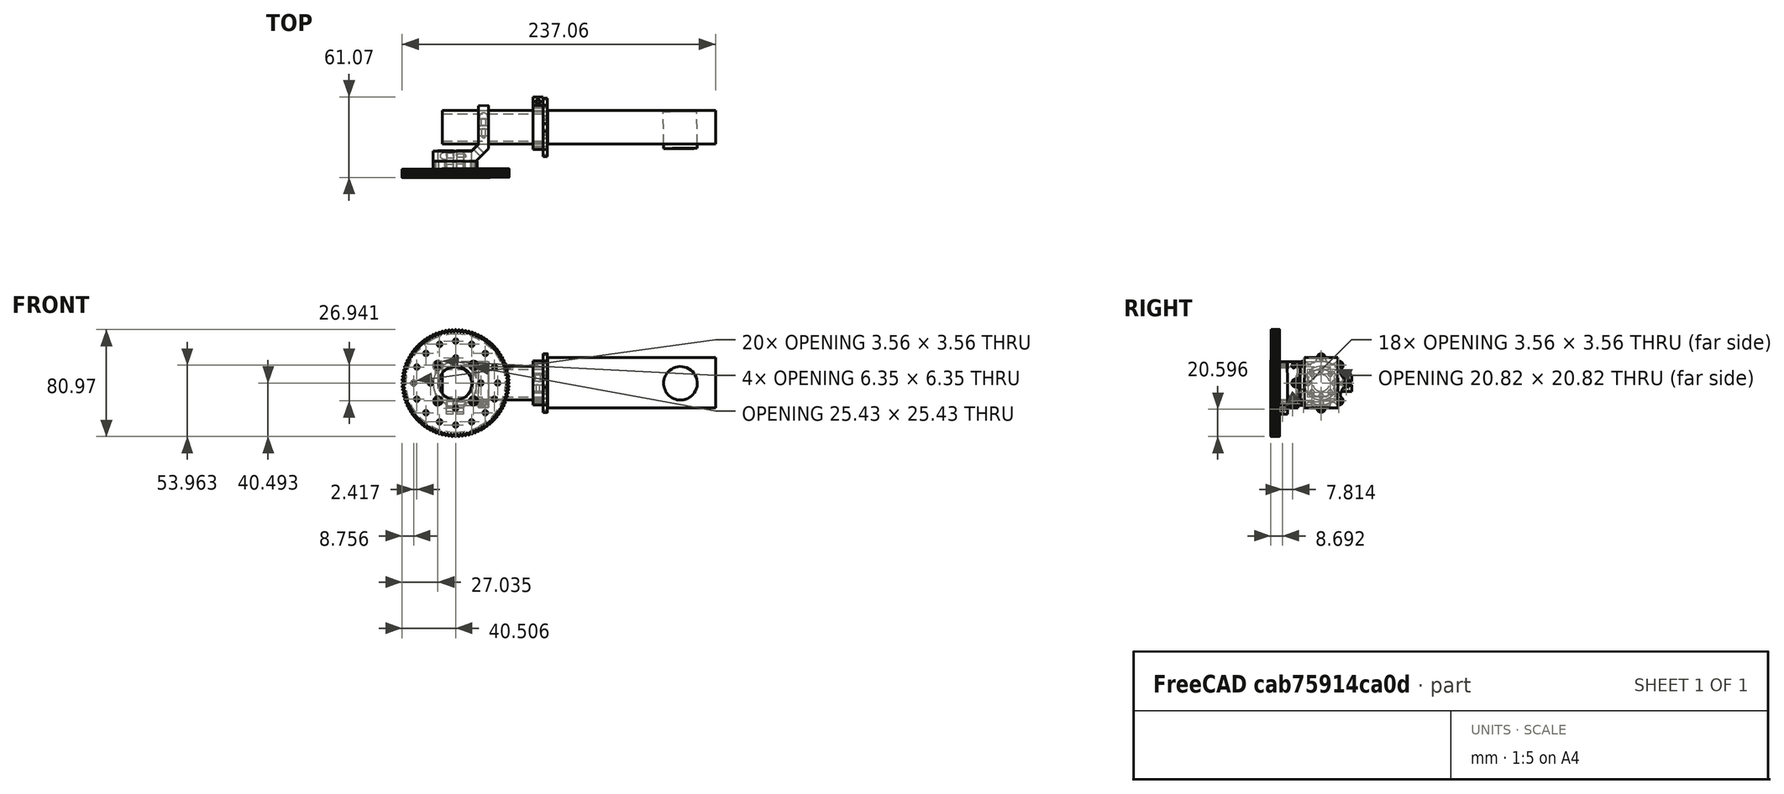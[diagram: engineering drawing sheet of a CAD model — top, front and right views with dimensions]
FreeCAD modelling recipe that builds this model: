
FCSTD DOCUMENT  (FreeCAD 0.15R4671 (Git))
Label: elbow
License: All rights reserved
LicenseURL: http://en.wikipedia.org/wiki/All_rights_reserved
objects: Part::Feature×6, Part::Box×1, Part::Cylinder×1
note: 8 computed .brp shape members not serialized (recipe doc carries the construction recipe); baked Part::Feature solids carry a one-line shape summary decoded from their .brp

FEATURE [Part::Feature] Part__Feature  label="635104"
  Placement = pos=(66.1451,36.2578,0) rot=(0,0,1;1.5708rad)
  shape: bbox 76.2 x 25.39 x 25.39 mm, 6 faces (baked)
FEATURE [Part::Feature] Part__Feature001  label="545354"
  Placement = pos=(66.1451,36.2578,0) rot=(0,0,1;1.5708rad)
  shape: bbox 7.62 x 39.7 x 33.29 mm, 45 faces (baked)
FEATURE [Part::Box] Box  label="Cube"
  Height = 38.1
  Length = 127
  Placement = pos=(69.559,23.557,-18.7554) rot=(0,0,1;0rad)
  Width = 25.4
FEATURE [Part::Cylinder] Cylinder
  Angle = 360
  Height = 27.94
  Placement = pos=(170.027,20.321,-0.182765) rot=(0.584444,-0.573279,-0.574261;4.18169rad)
  Radius = 12.7
FEATURE [Part::Feature] Part__Feature004  label="545388"
  Placement = pos=(69.3201,36.2578,0) rot=(0,0,1;1.5708rad)
  shape: bbox 3.175 x 44.37 x 44.37 mm, 73 faces (baked)
FEATURE [Part::Feature] Part__Feature005  label="545464"
  Placement = pos=(24.8701,36.2578,-9.63981e-06) rot=(0.579573,-0.579166,0.57329;2.10749rad)
  shape: bbox 41.96 x 42.27 x 35.28 mm, 62 faces (baked)
FEATURE [Part::Feature] Part__Feature006  label="615234"
  Placement = pos=(0,0,0) rot=(-0.000987,-0.000994,-0.999999;1.56718rad)
  shape: bbox 80.99 x 6.684 x 80.98 mm, 898 faces (baked)
FEATURE [Part::Feature] Part__Feature007  label="545352"
  Placement = pos=(-0.492574,3.13161,-0.459087) rot=(0,1,0;1.56789rad)
  shape: bbox 33.37 x 7.62 x 39.76 mm, 45 faces (baked)
